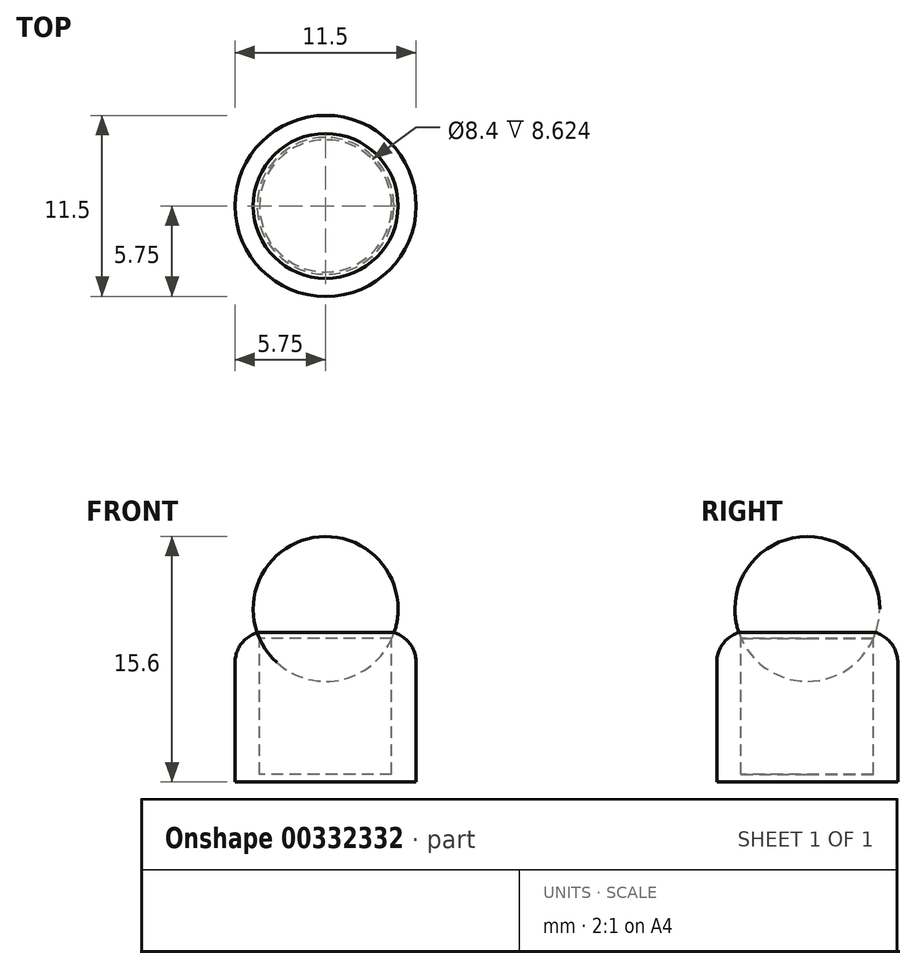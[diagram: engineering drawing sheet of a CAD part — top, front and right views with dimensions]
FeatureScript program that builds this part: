
annotation { "Feature Type Name" : "Feature", "Feature Type Description" : "" }
export const myFeature = defineFeature(function(context is Context, id is Id, definition is map)
    precondition{}
    {
        {
            var Q0;
            Q0=qCreatedBy(makeId("Top.planeOp"),FACE);
            var sketch = newSketch(context, id + "F0", { "sketchPlane" : qUnion([Q0])});
            skCircle(sketch, "E0", {"center": v(0, 0) * mm, "radius": 4.6 * mm});
            skLineSegment(sketch, "E1", {"start": v(0, 4.6) * mm, "end": v(0, -4.6) * mm});
            skCircle(sketch, "E2", {"center": v(0, 0) * mm, "radius": 5.75 * mm});
            skCircle(sketch, "E3", {"center": v(0, 0) * mm, "radius": 4.2 * mm});
            skSolve(sketch);
        }
        {
            var Q0;
            {var subQ0=sQuery(id+"F0.wireOp",EDGE,"E3");var subQ1=sQuery(id+"F0.wireOp",EDGE,"E1");var subQ2=makeQuery(id+"F0.imprint","INTERSECT",VERTEX,{"disambiguationData":[OD(0.0)],"derivedFrom":[subQ1,subQ0]});Q0=makeQuery(id+"F0.imprint","IMPRINT",FACE,{"disambiguationData":[TD([[makeQuery(id+"F0.imprint","IMPRINT",EDGE,{"disambiguationData":[TD([[subQ2,-1.0]])],"derivedFrom":subQ1}),-1.0]])]});}
            var Q1;
            {var subQ0=sQuery(id+"F0.wireOp",EDGE,"E1");var subQ1=sQuery(id+"F0.wireOp",EDGE,"E0");var subQ2=makeQuery(id+"F0.imprint","INTERSECT",VERTEX,{"disambiguationData":[OD(0.0)],"derivedFrom":[subQ1,subQ0]});Q1=makeQuery(id+"F0.imprint","IMPRINT",FACE,{"disambiguationData":[TD([[makeQuery(id+"F0.imprint","IMPRINT",EDGE,{"disambiguationData":[TD([[subQ2,-1.0]])],"derivedFrom":subQ1}),1.0]])]});}
            var Q2;
            Q2=sQuery(id+"F0.wireOp",EDGE,"E1");
            revolve(context, id + "F1", {"entities" : qUnion([Q0, Q1]), "axis" : qUnion([Q2]), "revolveType" : RevolveType.FULL});
        }
        {
            var Q0;
            {var subQ0=sQuery(id+"F0.wireOp",EDGE,"E3");var subQ1=sQuery(id+"F0.wireOp",EDGE,"E1");var subQ2=makeQuery(id+"F0.imprint","INTERSECT",VERTEX,{"disambiguationData":[OD(0.0)],"derivedFrom":[subQ1,subQ0]});Q0=makeQuery(id+"F0.imprint","IMPRINT",FACE,{"disambiguationData":[TD([[makeQuery(id+"F0.imprint","IMPRINT",EDGE,{"disambiguationData":[TD([[subQ2,-1.0]])],"derivedFrom":subQ1}),-1.0]])]});}
            var Q1;
            Q1=makeQuery(id+"F0.imprint","IMPRINT",FACE,{"disambiguationData":[TD([[makeQuery(id+"F0.imprint","IMPRINT",EDGE,{"derivedFrom":sQuery(id+"F0.wireOp",EDGE,"E2")}),1.0]])]});
            var Q2;
            {var subQ0=sQuery(id+"F0.wireOp",EDGE,"E1");var subQ1=sQuery(id+"F0.wireOp",EDGE,"E0");var subQ2=makeQuery(id+"F0.imprint","INTERSECT",VERTEX,{"disambiguationData":[OD(0.0)],"derivedFrom":[subQ1,subQ0]});Q2=makeQuery(id+"F0.imprint","IMPRINT",FACE,{"disambiguationData":[TD([[makeQuery(id+"F0.imprint","IMPRINT",EDGE,{"disambiguationData":[TD([[subQ2,-1.0]])],"derivedFrom":subQ1}),1.0]])]});}
            var Q3;
            {var subQ0=sQuery(id+"F0.wireOp",EDGE,"E3");var subQ1=sQuery(id+"F0.wireOp",EDGE,"E1");var subQ2=makeQuery(id+"F0.imprint","INTERSECT",VERTEX,{"disambiguationData":[OD(0.0)],"derivedFrom":[subQ1,subQ0]});Q3=makeQuery(id+"F0.imprint","IMPRINT",FACE,{"disambiguationData":[TD([[makeQuery(id+"F0.imprint","IMPRINT",EDGE,{"disambiguationData":[TD([[subQ2,-1.0]])],"derivedFrom":subQ1}),1.0]])]});}
            var Q4;
            {var subQ0=sQuery(id+"F0.wireOp",EDGE,"E1");var subQ1=sQuery(id+"F0.wireOp",EDGE,"E0");var subQ2=makeQuery(id+"F0.imprint","INTERSECT",VERTEX,{"disambiguationData":[OD(0.0)],"derivedFrom":[subQ1,subQ0]});Q4=makeQuery(id+"F0.imprint","IMPRINT",FACE,{"disambiguationData":[TD([[makeQuery(id+"F0.imprint","IMPRINT",EDGE,{"disambiguationData":[TD([[subQ2,1.0]])],"derivedFrom":subQ1}),1.0]])]});}
            extrude(context, id + "F2", {"entities" : qUnion([Q0, Q1, Q2, Q3, Q4]), "oppositeDirection" : true, "depth" : 11 * mm, "hasSecondDirection" : true, "secondDirectionOppositeDirection" : true, "secondDirectionDepth" : 1.5 * mm});
        }
        {
            var Q0;
            {var subQ0=sQuery(id+"F0.wireOp",EDGE,"E3");var subQ1=sQuery(id+"F0.wireOp",EDGE,"E1");var subQ2=makeQuery(id+"F0.imprint","INTERSECT",VERTEX,{"disambiguationData":[OD(0.0)],"derivedFrom":[subQ1,subQ0]});Q0=makeQuery(id+"F0.imprint","IMPRINT",FACE,{"disambiguationData":[TD([[makeQuery(id+"F0.imprint","IMPRINT",EDGE,{"disambiguationData":[TD([[subQ2,-1.0]])],"derivedFrom":subQ1}),-1.0]])]});}
            var Q1;
            {var subQ0=sQuery(id+"F0.wireOp",EDGE,"E3");var subQ1=sQuery(id+"F0.wireOp",EDGE,"E1");var subQ2=makeQuery(id+"F0.imprint","INTERSECT",VERTEX,{"disambiguationData":[OD(0.0)],"derivedFrom":[subQ1,subQ0]});Q1=makeQuery(id+"F0.imprint","IMPRINT",FACE,{"disambiguationData":[TD([[makeQuery(id+"F0.imprint","IMPRINT",EDGE,{"disambiguationData":[TD([[subQ2,-1.0]])],"derivedFrom":subQ1}),1.0]])]});}
            extrude(context, id + "F3", {"entities" : qUnion([Q0, Q1]), "operationType" : NewBodyOperationType.REMOVE, "oppositeDirection" : true, "depth" : 10.5 * mm});
        }
        {
            var Q0;
            Q0=makeQuery(id+"F1.opRevolve","SWEPT_BODY",BODY,{"disambiguationData":[OSD([sQuery(id+"F0.wireOp",EDGE,"E0"),sQuery(id+"F0.wireOp",EDGE,"E1")])]});
            var Q1;
            Q1=makeQuery(id+"F2.opExtrude","SWEPT_BODY",BODY,{"disambiguationData":[OSD([sQuery(id+"F0.wireOp",EDGE,"E2")])]});
            booleanBodies(context, id + "F4", {"operationType" : BooleanOperationType.SUBTRACTION, "tools" : qUnion([Q0]), "targets" : qUnion([Q1])});
        }
        {
            var Q0;
            Q0=makeQuery(id+"F2.opExtrude","CAP_EDGE",EDGE,{"disambiguationData":[OSD([sQuery(id+"F0.wireOp",EDGE,"E2")])],"isStart":true});
            fillet(context, id + "F5", {"entities" : qUnion([Q0]), "radius" : 2 * mm, "tangentPropagation" : true, "allowEdgeOverflow" : false});
        }
        {
            var Q0;
            {var subQ0=sQuery(id+"F0.wireOp",EDGE,"E3");var subQ1=sQuery(id+"F0.wireOp",EDGE,"E1");var subQ2=makeQuery(id+"F0.imprint","INTERSECT",VERTEX,{"disambiguationData":[OD(0.0)],"derivedFrom":[subQ1,subQ0]});Q0=makeQuery(id+"F0.imprint","IMPRINT",FACE,{"disambiguationData":[TD([[makeQuery(id+"F0.imprint","IMPRINT",EDGE,{"disambiguationData":[TD([[subQ2,-1.0]])],"derivedFrom":subQ1}),-1.0]])]});}
            var Q1;
            {var subQ0=sQuery(id+"F0.wireOp",EDGE,"E1");var subQ1=sQuery(id+"F0.wireOp",EDGE,"E0");var subQ2=makeQuery(id+"F0.imprint","INTERSECT",VERTEX,{"disambiguationData":[OD(0.0)],"derivedFrom":[subQ1,subQ0]});Q1=makeQuery(id+"F0.imprint","IMPRINT",FACE,{"disambiguationData":[TD([[makeQuery(id+"F0.imprint","IMPRINT",EDGE,{"disambiguationData":[TD([[subQ2,-1.0]])],"derivedFrom":subQ1}),1.0]])]});}
            var Q2;
            Q2=sQuery(id+"F0.wireOp",EDGE,"E1");
            revolve(context, id + "F6", {"entities" : qUnion([Q0, Q1]), "axis" : qUnion([Q2]), "revolveType" : RevolveType.FULL});
        }
    });
